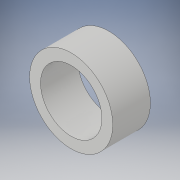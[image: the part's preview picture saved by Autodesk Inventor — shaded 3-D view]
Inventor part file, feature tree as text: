
AUTODESK INVENTOR PART (.ipt)
format: ipt  version: 2019 (Build 230136000, 136)  size: 102,912 bytes
history: native  units: mm
features: extrude x2, sketch x2
ambient origin geometry x8: Origin, YZ Plane, XZ Plane, XY Plane, X Axis, Y Axis, Z Axis, Center Point
bodies: Solid1 (feature_tree)
feature tree (4):
  extrude  "Extrusion1"  Depth=95.0mm TaperAngle=0.0deg
  extrude  "Extrusion2"  Depth=9.5mm TaperAngle=0.0deg
  sketch  "Sketch1"  dims[d0=210.0mm d1=95.0mm d2=0.0mm]
  sketch  "Sketch2"  dims[d3=155.0mm d4=9.5mm d5=0.0mm]
